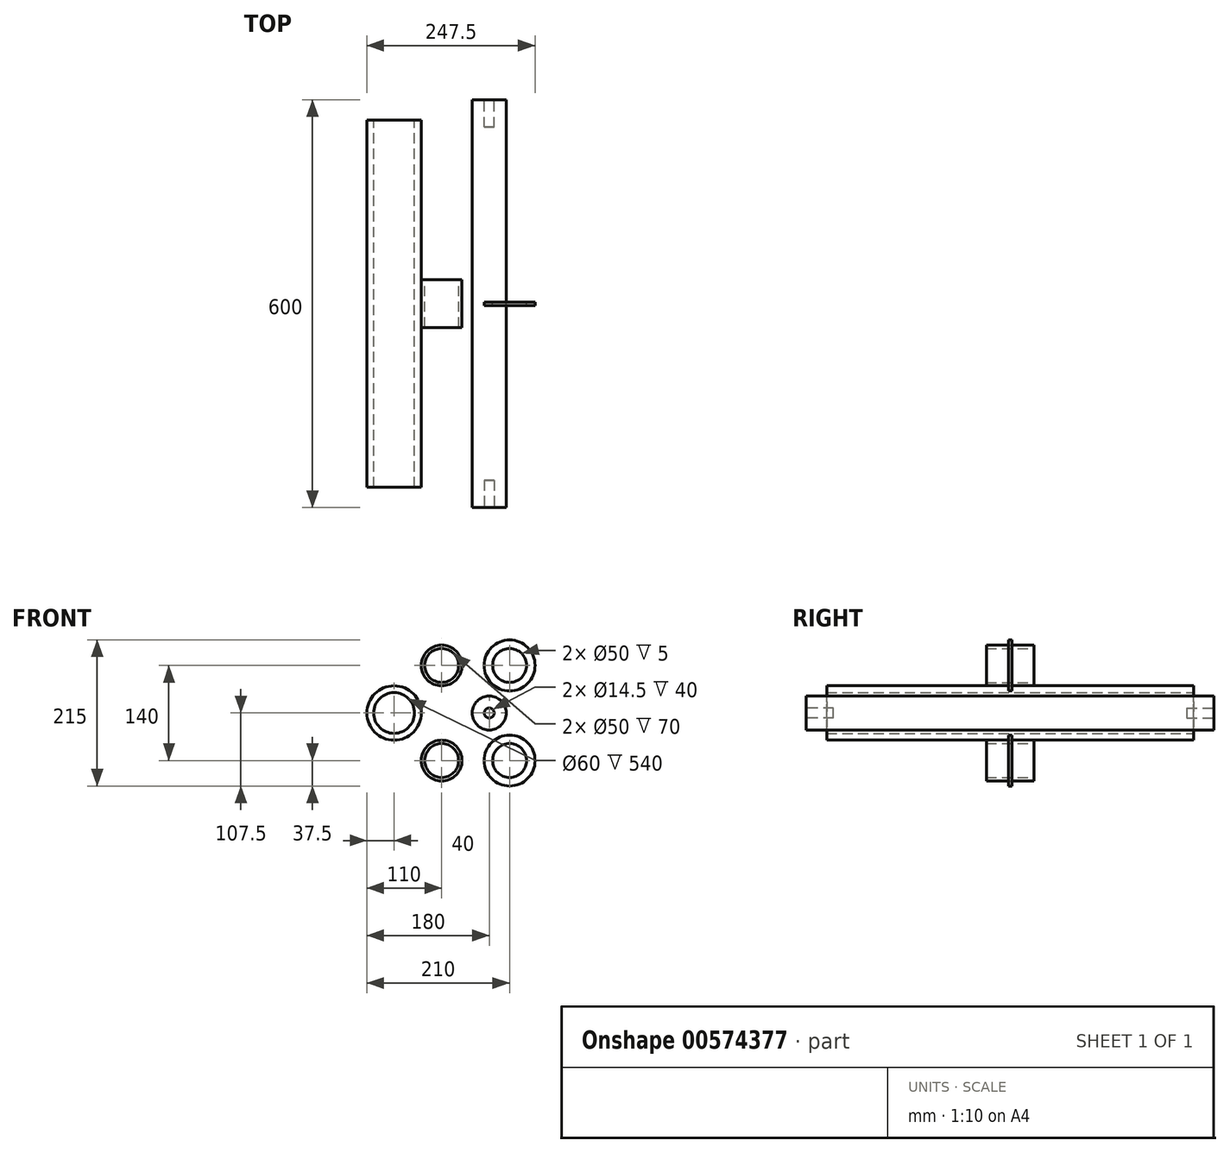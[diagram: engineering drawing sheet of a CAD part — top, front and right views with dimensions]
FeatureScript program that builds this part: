
annotation { "Feature Type Name" : "Feature", "Feature Type Description" : "" }
export const myFeature = defineFeature(function(context is Context, id is Id, definition is map)
    precondition{}
    {
        {
            var Q0;
            Q0=qCreatedBy(makeId("Front.planeOp"),FACE);
            var sketch = newSketch(context, id + "F0", { "sketchPlane" : qUnion([Q0])});
            skCircle(sketch, "E0", {"center": v(-70, 0) * mm, "radius": 40 * mm});
            skCircle(sketch, "E1", {"center": v(-70, 0) * mm, "radius": 30 * mm});
            skSolve(sketch);
        }
        {
            var Q0;
            Q0=makeQuery(id+"F0.imprint","IMPRINT",FACE,{"disambiguationData":[TD([[makeQuery(id+"F0.imprint","IMPRINT",EDGE,{"derivedFrom":sQuery(id+"F0.wireOp",EDGE,"E0")}),1.0]])]});
            extrude(context, id + "F1", {"entities" : qUnion([Q0]), "endBound" : BoundingType.SYMMETRIC, "depth" : 540 * mm, "offsetDistance" : 25 * mm});
        }
        {
            var Q0;
            Q0=qCreatedBy(makeId("Front.planeOp"),FACE);
            var sketch = newSketch(context, id + "F2", { "sketchPlane" : qUnion([Q0])});
            skCircle(sketch, "E2", {"center": v(0, 70) * mm, "radius": 30 * mm});
            skCircle(sketch, "E3", {"center": v(0, 70) * mm, "radius": 25 * mm});
            skCircle(sketch, "E4", {"center": v(0, -70) * mm, "radius": 30 * mm});
            skCircle(sketch, "E5", {"center": v(0, -70) * mm, "radius": 25 * mm});
            skSolve(sketch);
        }
        {
            var Q0;
            Q0=makeQuery(id+"F2.imprint","IMPRINT",FACE,{"disambiguationData":[TD([[makeQuery(id+"F2.imprint","IMPRINT",EDGE,{"derivedFrom":sQuery(id+"F2.wireOp",EDGE,"E2")}),1.0]])]});
            var Q1;
            Q1=makeQuery(id+"F2.imprint","IMPRINT",FACE,{"disambiguationData":[TD([[makeQuery(id+"F2.imprint","IMPRINT",EDGE,{"derivedFrom":sQuery(id+"F2.wireOp",EDGE,"E4")}),1.0]])]});
            extrude(context, id + "F3", {"entities" : qUnion([Q0, Q1]), "endBound" : BoundingType.SYMMETRIC, "depth" : 70 * mm, "offsetDistance" : 25 * mm});
        }
        {
            var Q0;
            Q0=qCreatedBy(makeId("Front.planeOp"),FACE);
            var sketch = newSketch(context, id + "F4", { "sketchPlane" : qUnion([Q0])});
            skCircle(sketch, "E6", {"center": v(70, 0) * mm, "radius": 25 * mm});
            skSolve(sketch);
        }
        {
            var Q0;
            Q0=makeQuery(id+"F4.imprint","IMPRINT",FACE,{"disambiguationData":[TD([[makeQuery(id+"F4.imprint","IMPRINT",EDGE,{"derivedFrom":sQuery(id+"F4.wireOp",EDGE,"E6")}),1.0]])]});
            extrude(context, id + "F5", {"entities" : qUnion([Q0]), "endBound" : BoundingType.SYMMETRIC, "depth" : 600 * mm, "offsetDistance" : 25 * mm});
        }
        {
            var Q0;
            Q0=qCreatedBy(makeId("Front.planeOp"),FACE);
            var sketch = newSketch(context, id + "F6", { "sketchPlane" : qUnion([Q0])});
            skCircle(sketch, "E7", {"center": v(100, 70) * mm, "radius": 37.5 * mm});
            skCircle(sketch, "E8", {"center": v(100, 70) * mm, "radius": 25 * mm});
            skCircle(sketch, "E9", {"center": v(100, -70) * mm, "radius": 37.5 * mm});
            skCircle(sketch, "E10", {"center": v(100, -70) * mm, "radius": 25 * mm});
            skSolve(sketch);
        }
        {
            var Q0;
            Q0=makeQuery(id+"F6.imprint","IMPRINT",FACE,{"disambiguationData":[TD([[makeQuery(id+"F6.imprint","IMPRINT",EDGE,{"derivedFrom":sQuery(id+"F6.wireOp",EDGE,"E7")}),1.0]])]});
            var Q1;
            Q1=makeQuery(id+"F6.imprint","IMPRINT",FACE,{"disambiguationData":[TD([[makeQuery(id+"F6.imprint","IMPRINT",EDGE,{"derivedFrom":sQuery(id+"F6.wireOp",EDGE,"E9")}),1.0]])]});
            extrude(context, id + "F7", {"entities" : qUnion([Q0, Q1]), "endBound" : BoundingType.SYMMETRIC, "depth" : 5 * mm, "offsetDistance" : 25 * mm});
        }
        {
            var Q0;
            Q0=makeQuery(id+"F5.opExtrude","CAP_FACE",FACE,{"disambiguationData":[OSD([sQuery(id+"F4.wireOp",EDGE,"E6")])],"isStart":false});
            var sketch = newSketch(context, id + "F8", { "sketchPlane" : qUnion([Q0])});
            skCircle(sketch, "E11.0.0", {"center": v(70, 0) * mm, "radius": 25 * mm});
            skCircle(sketch, "E12", {"center": v(70, 0) * mm, "radius": 7.25 * mm});
            skSolve(sketch);
        }
        {
            var Q0;
            Q0=makeQuery(id+"F8.imprint","IMPRINT",FACE,{"disambiguationData":[TD([[makeQuery(id+"F8.imprint","IMPRINT",EDGE,{"derivedFrom":sQuery(id+"F8.wireOp",EDGE,"E12")}),1.0]])]});
            extrude(context, id + "F9", {"entities" : qUnion([Q0]), "operationType" : NewBodyOperationType.REMOVE, "oppositeDirection" : true, "depth" : 40 * mm, "offsetDistance" : 25 * mm});
        }
        {
            var Q0;
            Q0=makeQuery(id+"F5.opExtrude","CAP_FACE",FACE,{"disambiguationData":[OSD([sQuery(id+"F4.wireOp",EDGE,"E6")])],"isStart":true});
            var sketch = newSketch(context, id + "F10", { "sketchPlane" : qUnion([Q0])});
            skCircle(sketch, "E13.0.0", {"center": v(-70, 0) * mm, "radius": 25 * mm});
            skCircle(sketch, "E14", {"center": v(-70, 0) * mm, "radius": 7.25 * mm});
            skSolve(sketch);
        }
        {
            var Q0;
            Q0=makeQuery(id+"F10.imprint","IMPRINT",FACE,{"disambiguationData":[TD([[makeQuery(id+"F10.imprint","IMPRINT",EDGE,{"derivedFrom":sQuery(id+"F10.wireOp",EDGE,"E14")}),1.0]])]});
            extrude(context, id + "F11", {"entities" : qUnion([Q0]), "operationType" : NewBodyOperationType.REMOVE, "oppositeDirection" : true, "depth" : 40 * mm, "offsetDistance" : 25 * mm});
        }
    });
